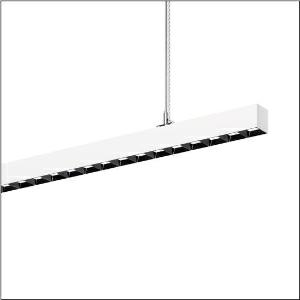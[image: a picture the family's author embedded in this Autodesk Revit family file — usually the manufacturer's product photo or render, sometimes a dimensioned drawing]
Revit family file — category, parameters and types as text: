
# Revit family: silica_r__21_51mx32tat7w_976d
name_source: partatom
category: Lighting Fixtures
units: mm (PartAtom-declared; Revit-internal decimal feet)

## family parameters
Cut with Voids When Loaded = No
Host = Face
Light Source = No
Part Type = Normal
Room Calculation Point = No
Round Connector Dimension = Use Diameter
Shared = No

## types (1)
- --- (1 x LED, 6220 lm, 53.4 W, 6500K)
    Apparent Load = 53 VA
    CIE Flux Codes = 84 99 100 60 100
    Color Rendering = 80
    Color Temperature = 6500K
    Default Elevation = 1800 mm
    Description = Silica® 21, office luminaire, primary light control with darklight reflector, of PMMA, black, CAT 2 (L<= 3000cd/m²), light emission: direct/indirect distribution, primary light characteristic: symmetric, installation type: suspended mounting, LED, rated luminous flux: 6.220lm, luminous efficacy: 111lm/W, light colour: 8tw, colour temperature: 2700..6500K, control gear: ECG DALI, with terminal, 3+2-pole, max. 2.5mm², mains connection: 220..240V, AC, 50/60Hz, rated input power: 56.1W, luminaire housing, of aluminium, traffic white (RAL 9016), length: 1.204mm, width: 53mm, height: 53mm, protection rating (complete): IP20, insulation class (complete): insulation class I (protective earthing), certification: CE, permissible operating ambient temperature: 0..+35°C, standard: EN 50419, packaging unit: 1 piece
    Height = 53 mm
    Lamp = 1 x LED
    Lamp Light Flux = 6220 lm
    Lamp Power = 53.4 W
    Lamp count = 1
    Length = 1204 mm
    Luminous efficacy = 116 lm/W
    Manufacturer = Siteco
    ModVariant = No
    Model = 51MX32TAT7W
    Mounting Place = Ceiling
    Mounting Type = Pendant
    Number of Poles = 1
    OnlyDefault = Yes
    Power Factor = 1
    Product Name = Silica® 21
    Product group = office luminaire | ceiling pendant
    ProductGroupID = 902
    Protection Class = Protection class I
    Protection Degree = IP 20
    RLX_Detail_Level = 1
    RLX_Emergency_Light_Flux = 0 lm
    RLX_Emergency_Type = 0
    RLX_Emergency_Type_DB = No
    RlxData = <blob elided: 40369 chars, md5=2db3ea4c>
    Socket = socket
    Standby Power = 0 W
    System Light Flux = 6220 lm
    System Power = 53 W
    Type Comments = individual setting
    Type Image = l_1297801.jpg
    URL = http://relux.com
    VarID = @adj_071287
    Voltage = 0 V
    Weight = 0.00 kg
    Width = 53 mm

## geometry (parser evidence)
native form markers: Blend x4, Sweep x10
no freeform markers — native parametric forms only
